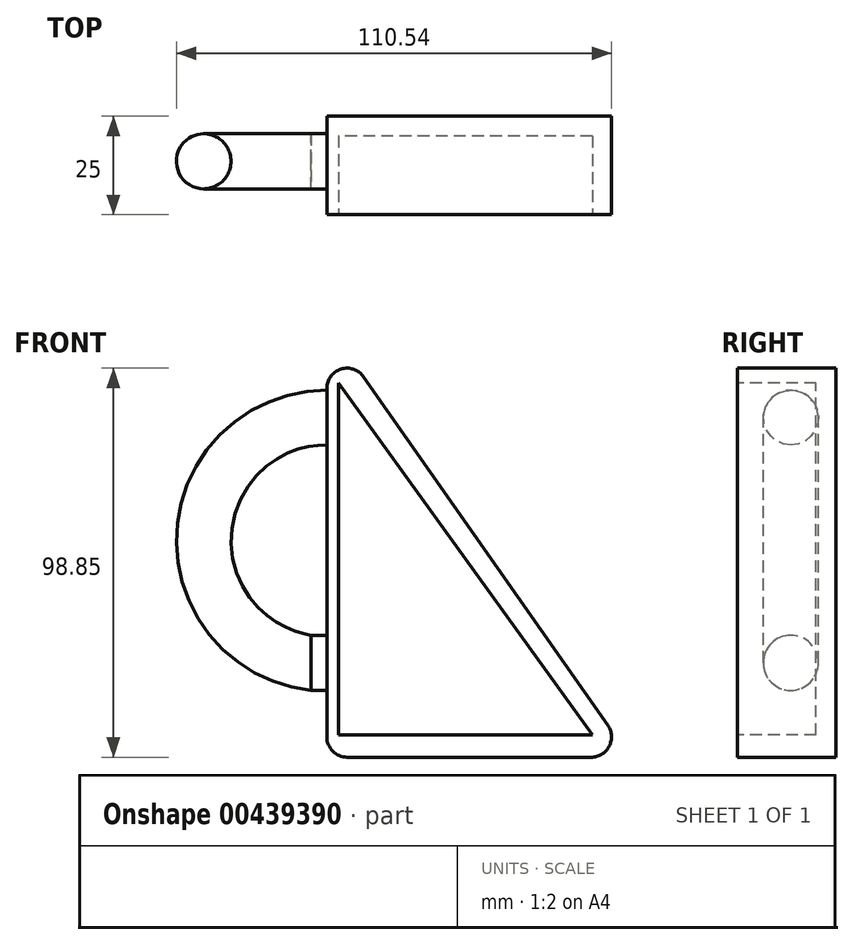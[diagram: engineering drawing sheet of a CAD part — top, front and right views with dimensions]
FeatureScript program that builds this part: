
annotation { "Feature Type Name" : "Feature", "Feature Type Description" : "" }
export const myFeature = defineFeature(function(context is Context, id is Id, definition is map)
    precondition{}
    {
        {
            var Q0;
            Q0=qCreatedBy(makeId("Front.planeOp"),FACE);
            var sketch = newSketch(context, id + "F0", { "sketchPlane" : qUnion([Q0])});
            skLineSegment(sketch, "E0", {"start": v(-36.6, 65.7) * mm, "end": v(-36.6, -44.33) * mm});
            skLineSegment(sketch, "E1", {"start": v(-36.6, -44.33) * mm, "end": v(40.44, -44.33) * mm});
            skLineSegment(sketch, "E2", {"start": v(40.44, -44.33) * mm, "end": v(-36.6, 65.7) * mm});
            skSolve(sketch);
        }
        {
            var Q0;
            Q0 = qSketchRegion(id + "F0", true);
            extrude(context, id + "F1", {"entities" : qUnion([Q0]), "depth" : 25 * mm});
        }
        {
            var Q0;
            Q0=makeQuery(id+"F1.opExtrude","CAP_FACE",FACE,{"disambiguationData":[OSD([sQuery(id+"F0.wireOp",EDGE,"E0"),sQuery(id+"F0.wireOp",EDGE,"E1"),sQuery(id+"F0.wireOp",EDGE,"E2")])],"isStart":false});
            var sketch = newSketch(context, id + "F2", { "sketchPlane" : qUnion([Q0])});
            skLineSegment(sketch, "E3", {"start": v(-33.6, 50.7) * mm, "end": v(-33.6, -38.71) * mm});
            skLineSegment(sketch, "E4", {"start": v(-33.6, -38.71) * mm, "end": v(30.86, -38.71) * mm});
            skLineSegment(sketch, "E5", {"start": v(30.86, -38.71) * mm, "end": v(-33.6, 50.7) * mm});
            skSolve(sketch);
        }
        {
            var Q0;
            Q0=makeQuery(id+"F2.imprint","IMPRINT",FACE,{"disambiguationData":[TD([[makeQuery(id+"F2.imprint","IMPRINT",EDGE,{"derivedFrom":sQuery(id+"F2.wireOp",EDGE,"E3")}),1.0]])]});
            extrude(context, id + "F3", {"entities" : qUnion([Q0]), "operationType" : NewBodyOperationType.REMOVE, "oppositeDirection" : true, "depth" : 20 * mm});
        }
        {
            var Q0;
            Q0=makeQuery(id+"F1.opExtrude","SWEPT_FACE",FACE,{"disambiguationData":[OSD([sQuery(id+"F0.wireOp",EDGE,"E0")])]});
            var sketch = newSketch(context, id + "F4", { "sketchPlane" : qUnion([Q0])});
            skCircle(sketch, "E6", {"center": v(11.44, -20.34) * mm, "radius": 7 * mm});
            skSolve(sketch);
        }
        {
            var Q0;
            Q0=makeQuery(id+"F4.imprint","IMPRINT",FACE,{"disambiguationData":[TD([[makeQuery(id+"F4.imprint","IMPRINT",EDGE,{"derivedFrom":sQuery(id+"F4.wireOp",EDGE,"E6")}),1.0]])]});
            extrude(context, id + "F5", {"entities" : qUnion([Q0]), "operationType" : NewBodyOperationType.ADD, "depth" : 4 * mm});
        }
        {
            var Q0;
            Q0=makeQuery(id+"F1.opExtrude","SWEPT_FACE",FACE,{"disambiguationData":[OSD([sQuery(id+"F0.wireOp",EDGE,"E0")])]});
            var sketch = newSketch(context, id + "F6", { "sketchPlane" : qUnion([Q0])});
            skLineSegment(sketch, "E7", {"start": v(25, 10.68) * mm, "end": v(0, 10.68) * mm});
            skSolve(sketch);
        }
        {
            var Q0;
            Q0=makeQuery(id+"F5.opExtrude","CAP_FACE",FACE,{"disambiguationData":[OSD([sQuery(id+"F4.wireOp",EDGE,"E6")])],"isStart":false});
            var Q1;
            Q1=sQuery(id+"F6.wireOp",EDGE,"E7");
            revolve(context, id + "F7", {"operationType" : NewBodyOperationType.ADD, "entities" : qUnion([Q0]), "axis" : qUnion([Q1]), "revolveType" : RevolveType.ONE_DIRECTION, "angle" : 175 * degree});
        }
        {
            var Q0;
            Q0=makeQuery(id+"F1.opExtrude","SWEPT_EDGE",EDGE,{"disambiguationData":[OSD([sQuery(id+"F0.wireOp",EDGE,"E1"),sQuery(id+"F0.wireOp",EDGE,"E2")])]});
            var Q1;
            Q1=makeQuery(id+"F1.opExtrude","SWEPT_EDGE",EDGE,{"disambiguationData":[OSD([sQuery(id+"F0.wireOp",EDGE,"E0"),sQuery(id+"F0.wireOp",EDGE,"E1")])]});
            var Q2;
            Q2=makeQuery(id+"F1.opExtrude","SWEPT_EDGE",EDGE,{"disambiguationData":[OSD([sQuery(id+"F0.wireOp",EDGE,"E0"),sQuery(id+"F0.wireOp",EDGE,"E2")])]});
            fillet(context, id + "F8", {"entities" : qUnion([Q0, Q1, Q2]), "radius" : 5.15 * mm, "tangentPropagation" : true, "allowEdgeOverflow" : false});
        }
    });
